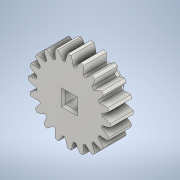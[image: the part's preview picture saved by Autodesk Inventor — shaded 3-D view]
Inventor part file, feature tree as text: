
AUTODESK INVENTOR PART (.ipt)
format: ipt  version: 2022 (Build 260153000, 153)  size: 544,768 bytes
history: native  units: mm (DEFAULTED — no unit token found)
features: sketch x4, extrude x3, plane x3, other x3, chamfer x2
ambient origin geometry x8: Origin, YZ Plane, XZ Plane, XY Plane, X Axis, Y Axis, Z Axis, Center Point
bodies: Solid1 (feature_tree)
feature tree (15):
  extrude  "Extrusion1"  Depth=6.35mm TaperAngle=0.0deg
  plane  "Work Plane1"
  plane  "Work Plane2"
  plane  "Work Plane3"
  other  "Spur Gear"
  extrude  "Extrusion2"  Depth=76.2mm TaperAngle=0.0deg
  extrude  "Extrusion3"  TaperAngle=0.0deg  [1 undecoded]
  chamfer  "Chamfer1"  Distance=25.4mm
  chamfer  "Chamfer2"  Distance=25.4mm
  sketch  "Sketch1"  dims[d0=22.8mm d1=6.35mm d2=0.0mm]
  sketch  "Sketch2"  dims[d3=20.0mm d4=76.2mm d5=0.0mm]
  other  "Srf1"
  sketch  "Sketch3"  dims[d6=0.0mm d7=1.570796mm d9=0.0mm d14=0.0mm d15=25.4mm]
  sketch  "Sketch4"  dims[d16=0.0mm d17=0.0mm d18=0.0mm d19=25.4mm d20=3.325mm d21=0.0mm d22=0.0mm d23=9.525mm d24=5.112mm d25=0.0mm d26=1.2mm d27=3.175mm d28=45.0deg d29=0.6mm d30=3.175mm d31=45.0deg]
  other  "Pitch Diameter"
note: 1 required parameter value undecoded (feature->parameter linkage not recoverable at this tier; creation-order binding heuristic only, values carry confidence <= 0.55)
